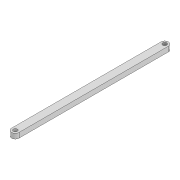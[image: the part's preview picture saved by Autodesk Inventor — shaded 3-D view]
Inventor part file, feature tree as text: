
AUTODESK INVENTOR PART (.ipt)
format: ipt  version: 2022 (Build 260153000, 153)  size: 89,088 bytes
history: native  units: mm
features: extrude x1, sketch x1
ambient origin geometry x8: Origin, YZ Plane, XZ Plane, XY Plane, X Axis, Y Axis, Z Axis, Center Point
bodies: Solid1 (feature_tree)
feature tree (2):
  extrude  "Extrusion1"  Depth=4.0mm
  sketch  "Sketch1"  dims[d0=3.2mm d1=3.2mm d2=6.0mm d3=120.239mm d6=4.0mm d7=0.0mm]
